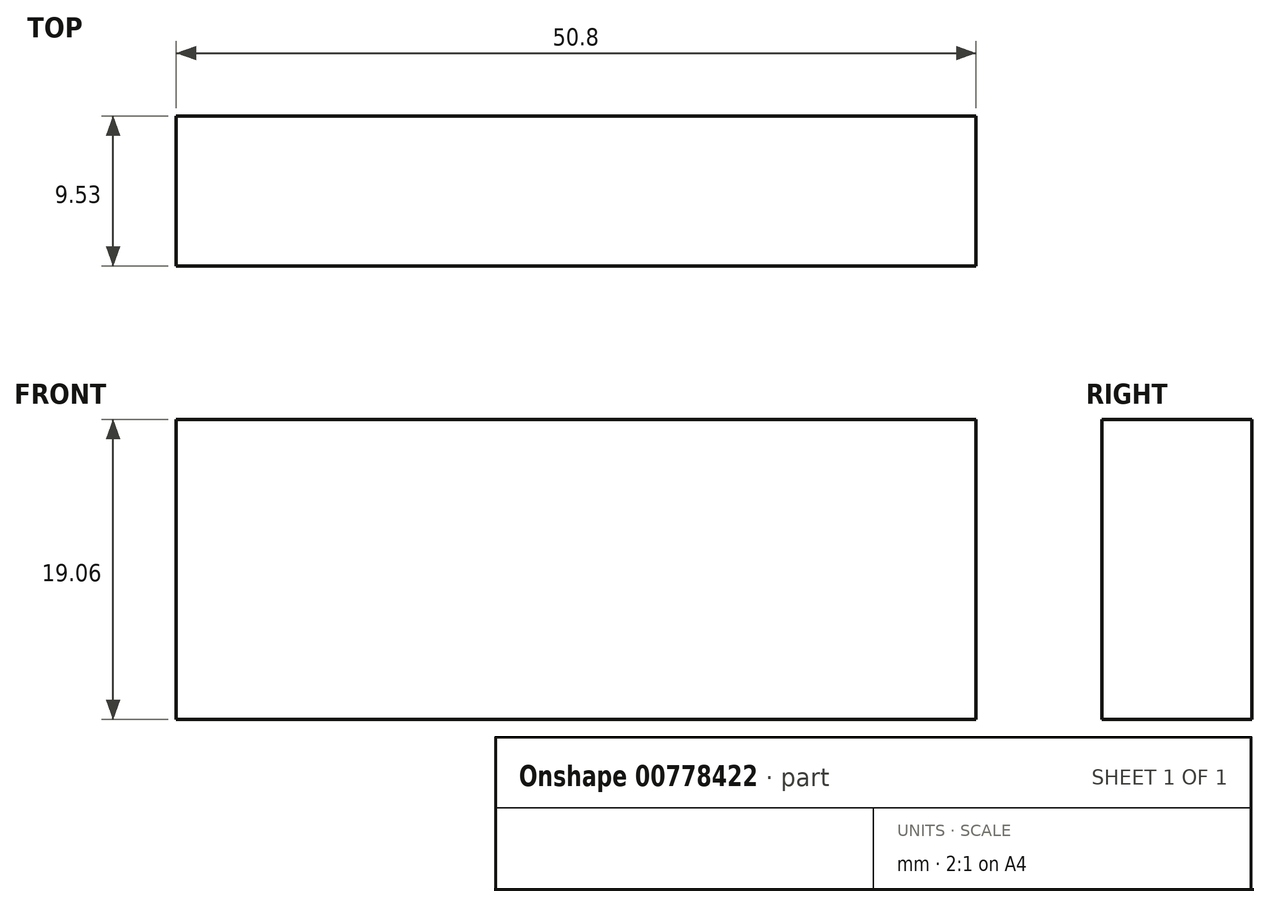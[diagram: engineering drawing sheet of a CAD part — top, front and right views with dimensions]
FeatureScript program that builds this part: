
annotation { "Feature Type Name" : "Feature", "Feature Type Description" : "" }
export const myFeature = defineFeature(function(context is Context, id is Id, definition is map)
    precondition{}
    {
        {
            var Q0;
            Q0=qCreatedBy(makeId("Front.planeOp"),FACE);
            var sketch = newSketch(context, id + "F0", { "sketchPlane" : qUnion([Q0])});
            skLineSegment(sketch, "E0.bottom", {"start": v(-25.4, -9.52) * mm, "end": v(25.4, -9.52) * mm});
            skLineSegment(sketch, "E0.top", {"start": v(-25.4, 9.52) * mm, "end": v(25.4, 9.52) * mm});
            skLineSegment(sketch, "E0.left", {"start": v(-25.4, -9.52) * mm, "end": v(-25.4, 9.52) * mm});
            skLineSegment(sketch, "E0.right", {"start": v(25.4, -9.52) * mm, "end": v(25.4, 9.52) * mm});
            skPoint(sketch, "E0.middle", {"position": v(0, 0) * mm});
            skSolve(sketch);
        }
        {
            var Q0;
            Q0=makeQuery(id+"F0.imprint","IMPRINT",FACE,{"disambiguationData":[TD([[makeQuery(id+"F0.imprint","IMPRINT",EDGE,{"derivedFrom":sQuery(id+"F0.wireOp",EDGE,"E0.bottom")}),1.0]])]});
            extrude(context, id + "F1", {"entities" : qUnion([Q0]), "depth" : 9.52 * mm, "offsetDistance" : 25.4 * mm});
        }
    });
